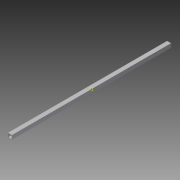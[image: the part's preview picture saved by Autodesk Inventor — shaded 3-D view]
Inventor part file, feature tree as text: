
AUTODESK INVENTOR PART (.ipt)
format: ipt  version: 2013 (Build 170138000, 138)  size: 73,216 bytes
history: native  units: in
note: dims shown in document units (in); Inventor stores cm internally (conversion verified against a paired STEP export)
features: extrude x1, plane x1, sketch x1
ambient origin geometry x8: Origin, YZ Plane, XZ Plane, XY Plane, X Axis, Y Axis, Z Axis, Center Point
bodies: Solid1 (feature_tree)
feature tree (3):
  extrude  "Extrusion1"  [1 undecoded]
  plane  "Work Plane1"
  sketch  "Sketch1"  dims[d0=70.35in d1=0.0in]
note: 1 required parameter value undecoded (feature->parameter linkage not recoverable at this tier; creation-order binding heuristic only, values carry confidence <= 0.55)
